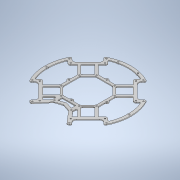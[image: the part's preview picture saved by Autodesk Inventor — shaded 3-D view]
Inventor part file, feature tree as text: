
AUTODESK INVENTOR PART (.ipt)
format: ipt  version: 2020 (Build 240168000, 168)  size: 1,229,824 bytes
history: native  units: mm
features: extrude x10, sketch x7, projected_geometry x6, other x1, fillet x1
ambient origin geometry x8: Origin, YZ Plane, XZ Plane, XY Plane, X Axis, Y Axis, Z Axis, Center Point
bodies: Body1 (feature_tree)
feature tree (25):
  other  "Твердое тело1"
  extrude  "outer"  TaperAngle=45.0deg  [1 undecoded]
  extrude  "inner"  Depth=7.0mm
  sketch  "Эскиз3"
  extrude  "Выдавливание3"  Depth=20.0mm
  extrude  "Выдавливание4"  Depth=7.0mm
  sketch  "Эскиз4"
  extrude  "Выдавливание5"  Depth=3.2mm
  extrude  "Выдавливание6"  Depth=59.0mm
  sketch  "Эскиз5"
  extrude  "Выдавливание7"  Depth=83.0mm
  extrude  "Выдавливание8"  Depth=69.0mm
  extrude  "Выдавливание9"  Depth=55.0mm
  extrude  "Выдавливание10"  Depth=3.0mm
  fillet  "Сопряжение1"  Radius=8.0mm
  sketch  "Эскиз1"
  sketch  "Эскиз2"
  projected_geometry  "Спроецированная петля1"
  projected_geometry  "Спроецированная петля2"
  projected_geometry  "Спроецированная петля3"
  projected_geometry  "Спроецированная петля4"
  sketch  "Эскиз6"
  projected_geometry  "Спроецированная петля5"
  sketch  "Эскиз7"
  projected_geometry  "Спроецированная петля6"
note: 1 required parameter value undecoded (feature->parameter linkage not recoverable at this tier; creation-order binding heuristic only, values carry confidence <= 0.55)
